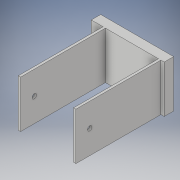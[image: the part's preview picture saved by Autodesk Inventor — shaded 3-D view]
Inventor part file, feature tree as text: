
AUTODESK INVENTOR PART (.ipt)
format: ipt  version: 2017 (Build 210142000, 142)  size: 120,832 bytes
history: native  units: in
note: dims shown in document units (in); Inventor stores cm internally (conversion verified against a paired STEP export)
features: extrude x4, sketch x4
ambient origin geometry x8: Origin, YZ Plane, XZ Plane, XY Plane, X Axis, Y Axis, Z Axis, Center Point
bodies: Solid1 (feature_tree)
feature tree (8):
  extrude  "Extrusion1"  Depth=2.5in
  extrude  "Extrusion2"  Depth=0.3in
  extrude  "Extrusion3"  Depth=4.5in TaperAngle=0.0deg
  extrude  "Extrusion4"  Depth=0.125in
  sketch  "Sketch1"  dims[d0=3.865in d1=2.5in]
  sketch  "Sketch2"  dims[d2=0.5in d3=0.0in d4=0.3in]
  sketch  "Sketch3"  dims[d5=0.125in d6=4.5in d7=0.0in]
  sketch  "Sketch4"  dims[d8=0.625in d9=0.125in d10=4.5in d11=0.0in d14=0.236in d15=4.0in d16=0.0in]
